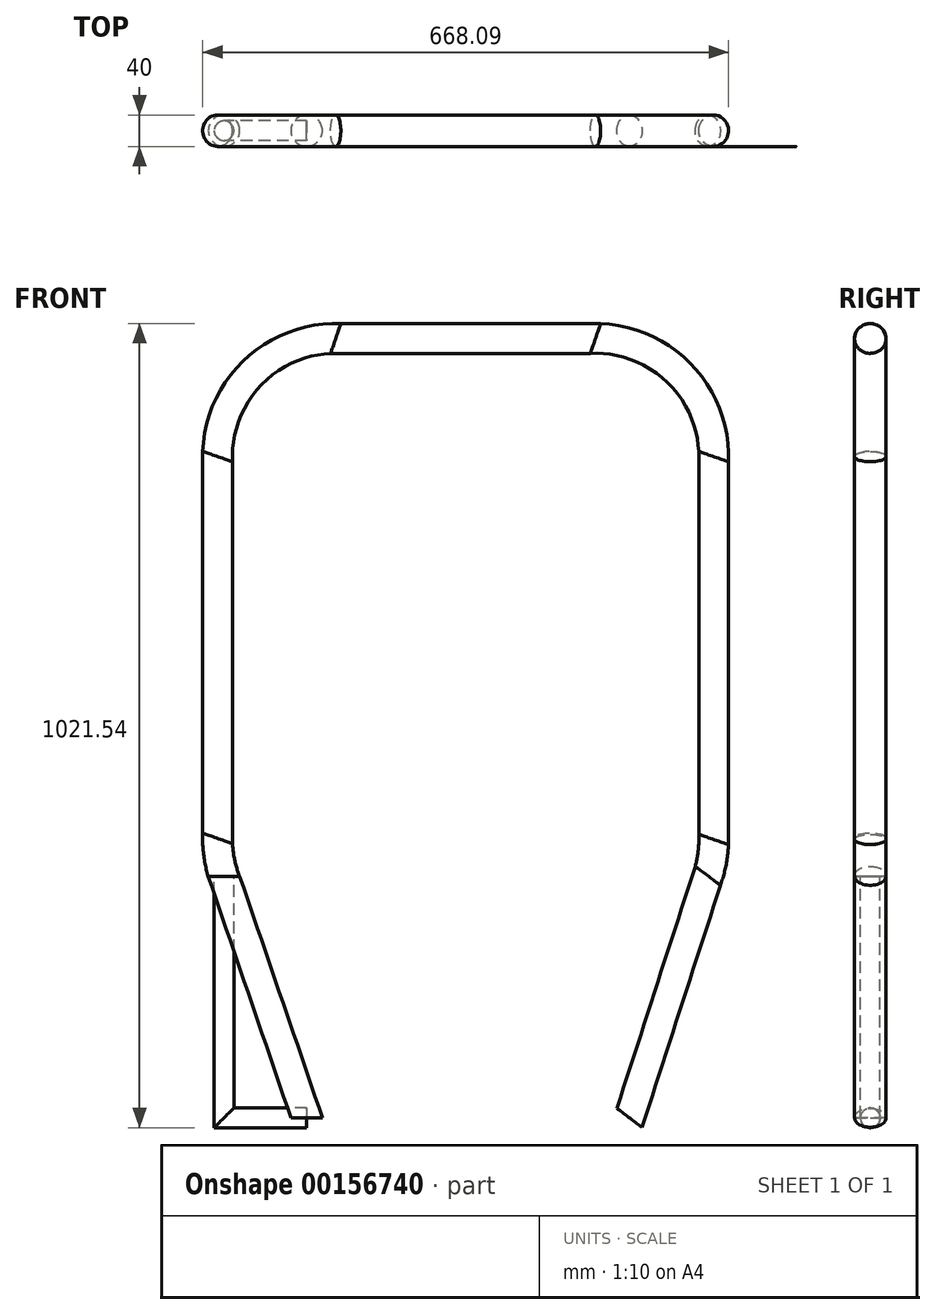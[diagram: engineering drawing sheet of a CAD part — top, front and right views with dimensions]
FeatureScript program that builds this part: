
annotation { "Feature Type Name" : "Feature", "Feature Type Description" : "" }
export const myFeature = defineFeature(function(context is Context, id is Id, definition is map)
    precondition{}
    {
        {
            var Q0;
            Q0=qCreatedBy(makeId("Front.planeOp"),FACE);
            var sketch = newSketch(context, id + "F0", { "sketchPlane" : qUnion([Q0])});
            skLineSegment(sketch, "E0", {"start": v(-205, 0) * mm, "end": v(-310.03, 306.35) * mm});
            skLineSegment(sketch, "E1", {"start": v(-318.14, 355) * mm, "end": v(-318.14, 840) * mm});
            skLineSegment(sketch, "E2", {"start": v(-168.14, 990) * mm, "end": v(161.86, 990) * mm});
            skLineSegment(sketch, "E3", {"start": v(311.86, 840) * mm, "end": v(311.86, 353.68) * mm});
            skLineSegment(sketch, "E4", {"start": v(304.56, 307.47) * mm, "end": v(205, 0) * mm});
            skPoint(sketch, "E5.visualSharp", {"position": v(-318.14, 990) * mm});
            skArc(sketch, "E5.filletArc", {"start": v(-168.14, 990) * mm, "mid": v(-274.2, 946.07) * mm, "end": v(-318.14, 840) * mm});
            skPoint(sketch, "E6.visualSharp", {"position": v(311.86, 990) * mm});
            skArc(sketch, "E6.filletArc", {"start": v(311.86, 840) * mm, "mid": v(267.92, 946.07) * mm, "end": v(161.86, 990) * mm});
            skPoint(sketch, "E7.visualSharp", {"position": v(-318.14, 330) * mm});
            skArc(sketch, "E7.filletArc", {"start": v(-318.14, 355) * mm, "mid": v(-316.1, 330.34) * mm, "end": v(-310.03, 306.35) * mm});
            skPoint(sketch, "E8.visualSharp", {"position": v(311.86, 330) * mm});
            skArc(sketch, "E8.filletArc", {"start": v(304.56, 307.47) * mm, "mid": v(310.02, 330.29) * mm, "end": v(311.86, 353.68) * mm});
            skSolve(sketch);
        }
        {
            var Q0;
            Q0=qCreatedBy(makeId("Top.planeOp"),FACE);
            var sketch = newSketch(context, id + "F1", { "sketchPlane" : qUnion([Q0])});
            skCircle(sketch, "E9", {"center": v(-205, 0) * mm, "radius": 20 * mm});
            skSolve(sketch);
        }
        {
            var Q0;
            Q0=makeQuery(id+"F1.imprint","IMPRINT",FACE,{"disambiguationData":[TD([[makeQuery(id+"F1.imprint","IMPRINT",EDGE,{"derivedFrom":sQuery(id+"F1.wireOp",EDGE,"E9")}),1.0]])]});
            var Q1;
            Q1=sQuery(id+"F0.wireOp",EDGE,"E0");
            var Q2;
            Q2=sQuery(id+"F0.wireOp",EDGE,"E7.filletArc");
            var Q3;
            Q3=sQuery(id+"F0.wireOp",EDGE,"E1");
            var Q4;
            Q4=sQuery(id+"F0.wireOp",EDGE,"E5.filletArc");
            var Q5;
            Q5=sQuery(id+"F0.wireOp",EDGE,"E2");
            var Q6;
            Q6=sQuery(id+"F0.wireOp",EDGE,"E6.filletArc");
            var Q7;
            Q7=sQuery(id+"F0.wireOp",EDGE,"E3");
            var Q8;
            Q8=sQuery(id+"F0.wireOp",EDGE,"E8.filletArc");
            var Q9;
            Q9=sQuery(id+"F0.wireOp",EDGE,"E4");
            sweep(context, id + "F2", {"profiles" : qUnion([Q0]), "path" : qUnion([Q1, Q2, Q3, Q4, Q5, Q6, Q7, Q8, Q9])});
        }
        {
            var Q0;
            Q0=qCreatedBy(makeId("Front.planeOp"),FACE);
            var sketch = newSketch(context, id + "F3", { "sketchPlane" : qUnion([Q0])});
            skLineSegment(sketch, "E10", {"start": v(-310.03, 306.35) * mm, "end": v(-310.03, 0) * mm});
            skLineSegment(sketch, "E11", {"start": v(-310.03, 0) * mm, "end": v(-205, 0) * mm});
            skSolve(sketch);
        }
        {
            var Q0;
            Q0=qCreatedBy(makeId("Right.planeOp"),FACE);
            var Q1;
            Q1=sQuery(id+"F3.wireOp",VERTEX,"E11.end");
            cPlane(context, id + "F4", {"entities" : qUnion([Q0, Q1]), "cplaneType" : CPlaneType.PLANE_POINT, "offset" : 25 * mm, "width" : 150 * mm, "height" : 150 * mm});
        }
        {
            var Q0;
            Q0=qCreatedBy(id+"F4.planeOp",FACE);
            var sketch = newSketch(context, id + "F5", { "sketchPlane" : qUnion([Q0])});
            skCircle(sketch, "E12", {"center": v(0, 0) * mm, "radius": 12.5 * mm});
            skSolve(sketch);
        }
        {
            var Q0;
            Q0=makeQuery(id+"F5.imprint","IMPRINT",FACE,{"disambiguationData":[TD([[makeQuery(id+"F5.imprint","IMPRINT",EDGE,{"derivedFrom":sQuery(id+"F5.wireOp",EDGE,"E12")}),1.0]])]});
            var Q1;
            Q1=sQuery(id+"F3.wireOp",EDGE,"E11");
            var Q2;
            Q2=sQuery(id+"F3.wireOp",EDGE,"E10");
            sweep(context, id + "F6", {"profiles" : qUnion([Q0]), "path" : qUnion([Q1, Q2])});
        }
    });
